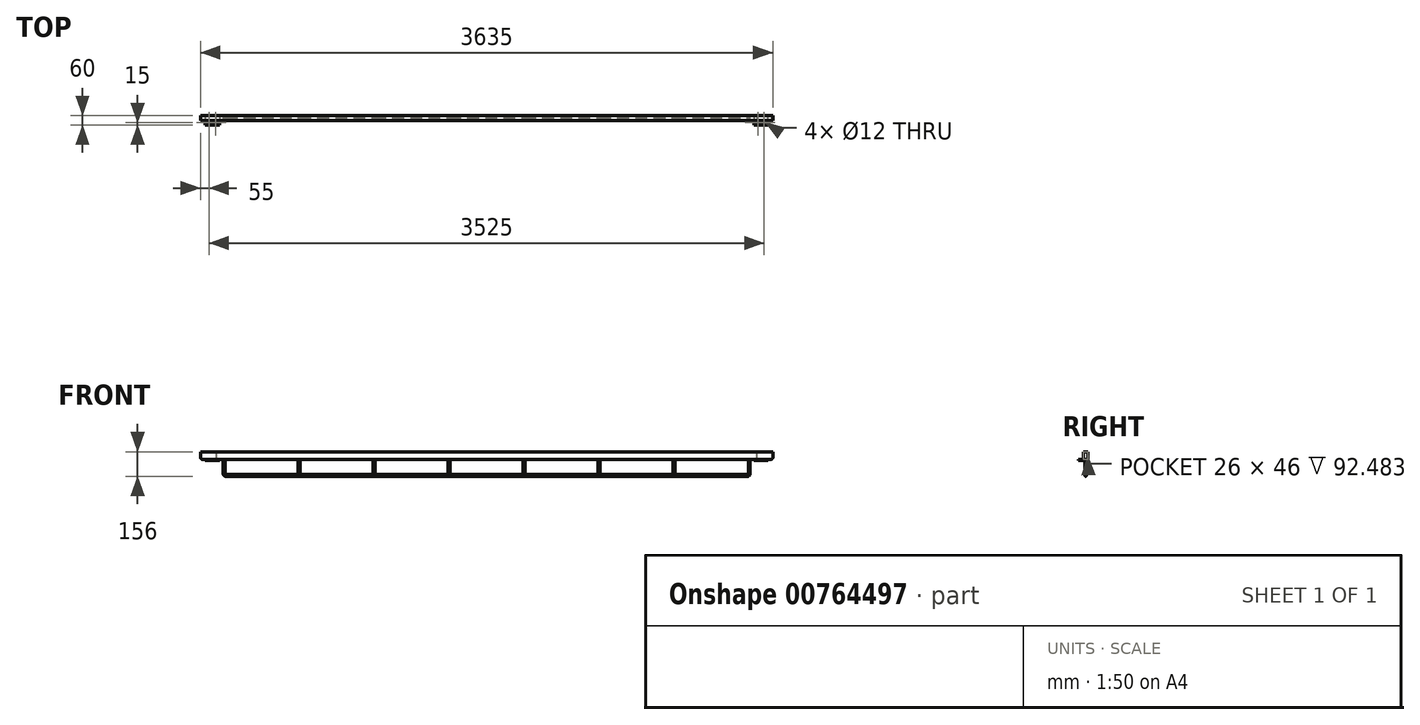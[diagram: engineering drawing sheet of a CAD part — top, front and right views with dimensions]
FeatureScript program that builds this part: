
annotation { "Feature Type Name" : "Feature", "Feature Type Description" : "" }
export const myFeature = defineFeature(function(context is Context, id is Id, definition is map)
    precondition{}
    {
        {
            var Q0;
            Q0=qCreatedBy(makeId("Front.planeOp"),FACE);
            var sketch = newSketch(context, id + "F0", { "sketchPlane" : qUnion([Q0])});
            skLineSegment(sketch, "E0.bottom", {"start": v(1787.5, -25) * mm, "end": v(-1787.5, -25) * mm});
            skLineSegment(sketch, "E0.top", {"start": v(1787.5, 25) * mm, "end": v(-1787.5, 25) * mm});
            skLineSegment(sketch, "E0.left", {"start": v(1787.5, -25) * mm, "end": v(1787.5, 25) * mm});
            skLineSegment(sketch, "E0.right", {"start": v(-1787.5, -25) * mm, "end": v(-1787.5, 25) * mm});
            skPoint(sketch, "E0.middle", {"position": v(0, 0) * mm});
            skSolve(sketch);
        }
        {
            var Q0;
            Q0 = qSketchRegion(id + "F0", true);
            extrude(context, id + "F1", {"entities" : qUnion([Q0]), "depth" : 15 * mm, "offsetDistance" : 25 * mm, "hasSecondDirection" : true, "secondDirectionOppositeDirection" : true, "secondDirectionDepth" : 15 * mm});
        }
        {
            var Q0;
            Q0=makeQuery(id+"F1.opExtrude","SWEPT_FACE",FACE,{"disambiguationData":[OSD([sQuery(id+"F0.wireOp",EDGE,"E0.bottom")])]});
            var sketch = newSketch(context, id + "F2", { "sketchPlane" : qUnion([Q0])});
            skLineSegment(sketch, "E1.0", {"start": v(-1787.5, 15) * mm, "end": v(-1787.5, -15) * mm});
            skLineSegment(sketch, "E2.bottom", {"start": v(-1787.5, -15) * mm, "end": v(-1697.5, -15) * mm});
            skLineSegment(sketch, "E2.top", {"start": v(-1787.5, 45) * mm, "end": v(-1697.5, 45) * mm});
            skLineSegment(sketch, "E2.left", {"start": v(-1787.5, -15) * mm, "end": v(-1787.5, 45) * mm});
            skLineSegment(sketch, "E2.right", {"start": v(-1697.5, -15) * mm, "end": v(-1697.5, 45) * mm});
            skSolve(sketch);
        }
        {
            var Q0;
            Q0 = qSketchRegion(id + "F2", true);
            extrude(context, id + "F3", {"entities" : qUnion([Q0]), "operationType" : NewBodyOperationType.ADD, "depth" : 5 * mm, "offsetDistance" : 25 * mm});
        }
        {
            var Q0;
            Q0=makeQuery(id+"F1.opExtrude","SWEPT_FACE",FACE,{"disambiguationData":[OSD([sQuery(id+"F0.wireOp",EDGE,"E0.bottom")])]});
            var sketch = newSketch(context, id + "F4", { "sketchPlane" : qUnion([Q0])});
            skLineSegment(sketch, "E3.0", {"start": v(1787.5, 15) * mm, "end": v(1787.5, -15) * mm});
            skLineSegment(sketch, "E4.bottom", {"start": v(1787.5, -15) * mm, "end": v(1697.5, -15) * mm});
            skLineSegment(sketch, "E4.top", {"start": v(1787.5, 45) * mm, "end": v(1697.5, 45) * mm});
            skLineSegment(sketch, "E4.left", {"start": v(1787.5, -15) * mm, "end": v(1787.5, 45) * mm});
            skLineSegment(sketch, "E4.right", {"start": v(1697.5, -15) * mm, "end": v(1697.5, 45) * mm});
            skSolve(sketch);
        }
        {
            var Q0;
            Q0 = qSketchRegion(id + "F4", true);
            extrude(context, id + "F5", {"entities" : qUnion([Q0]), "operationType" : NewBodyOperationType.ADD, "depth" : 5 * mm, "offsetDistance" : 25 * mm});
        }
        {
            var Q0;
            Q0=makeQuery(id+"F3.opExtrude","CAP_FACE",FACE,{"disambiguationData":[OSD([sQuery(id+"F2.wireOp",EDGE,"E2.bottom"),sQuery(id+"F2.wireOp",EDGE,"E2.top"),sQuery(id+"F2.wireOp",EDGE,"E2.left"),sQuery(id+"F2.wireOp",EDGE,"E2.right")])],"isStart":false});
            var sketch = newSketch(context, id + "F6", { "sketchPlane" : qUnion([Q0])});
            skCircle(sketch, "E5.0", {"center": v(-935, 30) * mm, "radius": 6 * mm});
            skCircle(sketch, "E6.0", {"center": v(-975, 30) * mm, "radius": 6 * mm});
            skSolve(sketch);
        }
        {
            var Q0;
            Q0 = qSketchRegion(id + "F6", true);
            var Q1;
            Q1=makeQuery(id+"F3.opExtrude","CAP_FACE",FACE,{"disambiguationData":[OSD([sQuery(id+"F2.wireOp",EDGE,"E2.bottom"),sQuery(id+"F2.wireOp",EDGE,"E2.top"),sQuery(id+"F2.wireOp",EDGE,"E2.left"),sQuery(id+"F2.wireOp",EDGE,"E2.right")])],"isStart":true});
            extrude(context, id + "F7", {"entities" : qUnion([Q0]), "operationType" : NewBodyOperationType.REMOVE, "endBound" : BoundingType.UP_TO_SURFACE, "oppositeDirection" : true, "depth" : 25 * mm, "endBoundEntityFace" : qUnion([Q1]), "offsetDistance" : 25 * mm});
        }
        {
            var Q0;
            Q0=makeQuery(id+"F5.opExtrude","CAP_FACE",FACE,{"disambiguationData":[OSD([sQuery(id+"F4.wireOp",EDGE,"E4.bottom"),sQuery(id+"F4.wireOp",EDGE,"E4.top"),sQuery(id+"F4.wireOp",EDGE,"E4.left"),sQuery(id+"F4.wireOp",EDGE,"E4.right")])],"isStart":false});
            var sketch = newSketch(context, id + "F8", { "sketchPlane" : qUnion([Q0])});
            skCircle(sketch, "E7.0", {"center": v(1762.5, 30) * mm, "radius": 6 * mm});
            skCircle(sketch, "E8.0", {"center": v(1722.5, 30) * mm, "radius": 6 * mm});
            skSolve(sketch);
        }
        {
            var Q0;
            Q0 = qSketchRegion(id + "F8", true);
            var Q1;
            Q1=makeQuery(id+"F5.opExtrude","CAP_FACE",FACE,{"disambiguationData":[OSD([sQuery(id+"F4.wireOp",EDGE,"E4.bottom"),sQuery(id+"F4.wireOp",EDGE,"E4.top"),sQuery(id+"F4.wireOp",EDGE,"E4.left"),sQuery(id+"F4.wireOp",EDGE,"E4.right")])],"isStart":true});
            extrude(context, id + "F9", {"entities" : qUnion([Q0]), "operationType" : NewBodyOperationType.REMOVE, "endBound" : BoundingType.UP_TO_SURFACE, "oppositeDirection" : true, "depth" : 25 * mm, "endBoundEntityFace" : qUnion([Q1]), "offsetDistance" : 25 * mm});
        }
        {
            var Q0;
            Q0=makeQuery(id+"F1.opExtrude","SWEPT_FACE",FACE,{"disambiguationData":[OSD([sQuery(id+"F0.wireOp",EDGE,"E0.bottom")])]});
            var sketch = newSketch(context, id + "F10", { "sketchPlane" : qUnion([Q0])});
            skLineSegment(sketch, "E9", {"start": v(-1697.5, -15) * mm, "end": v(-1667.5, -15) * mm, "construction": true});
            skLineSegment(sketch, "E10", {"start": v(-1667.5, -15) * mm, "end": v(-1667.5, 15) * mm, "construction": true});
            skCircle(sketch, "E11", {"center": v(-1667.5, 0) * mm, "radius": 6 * mm});
            skLineSegment(sketch, "E12", {"start": v(1697.5, -15) * mm, "end": v(1667.5, -15) * mm, "construction": true});
            skLineSegment(sketch, "E13", {"start": v(1667.5, -15) * mm, "end": v(1667.5, 15) * mm, "construction": true});
            skCircle(sketch, "E14", {"center": v(1667.5, 0) * mm, "radius": 6 * mm});
            skLineSegment(sketch, "E15", {"start": v(1667.5, 0) * mm, "end": v(1191.07, 0) * mm});
            skLineSegment(sketch, "E16", {"start": v(1191.07, 0) * mm, "end": v(714.64, 0) * mm});
            skLineSegment(sketch, "E17", {"start": v(714.64, 0) * mm, "end": v(238.21, 0) * mm});
            skLineSegment(sketch, "E18", {"start": v(238.21, 0) * mm, "end": v(-238.21, 0) * mm});
            skLineSegment(sketch, "E19", {"start": v(-238.21, 0) * mm, "end": v(-714.64, 0) * mm});
            skLineSegment(sketch, "E20", {"start": v(-714.64, 0) * mm, "end": v(-1191.07, 0) * mm});
            skLineSegment(sketch, "E21", {"start": v(-1667.5, 0) * mm, "end": v(-1191.07, 0) * mm});
            skCircle(sketch, "E22", {"center": v(-1191.07, 0) * mm, "radius": 6 * mm});
            skCircle(sketch, "E23", {"center": v(-714.64, 0) * mm, "radius": 6 * mm});
            skCircle(sketch, "E24", {"center": v(-238.21, 0) * mm, "radius": 6 * mm});
            skCircle(sketch, "E25", {"center": v(238.21, 0) * mm, "radius": 6 * mm});
            skCircle(sketch, "E26", {"center": v(714.64, 0) * mm, "radius": 6 * mm});
            skCircle(sketch, "E27", {"center": v(1191.07, 0) * mm, "radius": 6 * mm});
            skSolve(sketch);
        }
        {
            var Q0;
            Q0=qCreatedBy(makeId("Front.planeOp"),FACE);
            var sketch = newSketch(context, id + "F11", { "sketchPlane" : qUnion([Q0])});
            skLineSegment(sketch, "E28.0", {"start": v(-1667.5, -25) * mm, "end": v(-1191.07, -25) * mm});
            skLineSegment(sketch, "E29.0", {"start": v(-714.64, -25) * mm, "end": v(-1191.07, -25) * mm});
            skLineSegment(sketch, "E30.0", {"start": v(-238.21, -25) * mm, "end": v(-714.64, -25) * mm});
            skLineSegment(sketch, "E31.0", {"start": v(238.21, -25) * mm, "end": v(-238.21, -25) * mm});
            skLineSegment(sketch, "E32.0", {"start": v(714.64, -25) * mm, "end": v(238.21, -25) * mm});
            skLineSegment(sketch, "E33.0", {"start": v(1191.07, -25) * mm, "end": v(714.64, -25) * mm});
            skLineSegment(sketch, "E34.0", {"start": v(1667.5, -25) * mm, "end": v(1191.07, -25) * mm});
            skLineSegment(sketch, "E35", {"start": v(1667.5, -25) * mm, "end": v(1667.5, -115) * mm});
            skLineSegment(sketch, "E36", {"start": v(1667.5, -115) * mm, "end": v(1657.5, -115) * mm});
            skArc(sketch, "E37", {"start": v(1657.5, -125) * mm, "mid": v(1664.57, -122.07) * mm, "end": v(1667.5, -115) * mm});
            skLineSegment(sketch, "E38", {"start": v(1657.5, -115) * mm, "end": v(1657.5, -125) * mm, "construction": true});
            skLineSegment(sketch, "E39", {"start": v(-1667.5, -25) * mm, "end": v(-1667.5, -115) * mm});
            skLineSegment(sketch, "E40", {"start": v(-1667.5, -115) * mm, "end": v(-1657.5, -115) * mm});
            skArc(sketch, "E41", {"start": v(-1667.5, -115) * mm, "mid": v(-1664.57, -122.07) * mm, "end": v(-1657.5, -125) * mm});
            skLineSegment(sketch, "E42", {"start": v(-1657.5, -115) * mm, "end": v(-1657.5, -125) * mm, "construction": true});
            skLineSegment(sketch, "E43", {"start": v(-1657.5, -125) * mm, "end": v(1657.5, -125) * mm});
            skLineSegment(sketch, "E44", {"start": v(1191.07, -25) * mm, "end": v(1191.07, -125) * mm});
            skLineSegment(sketch, "E45", {"start": v(714.64, -25) * mm, "end": v(714.64, -125) * mm});
            skLineSegment(sketch, "E46", {"start": v(238.21, -25) * mm, "end": v(238.21, -125) * mm});
            skLineSegment(sketch, "E47", {"start": v(-238.21, -25) * mm, "end": v(-238.21, -125) * mm});
            skLineSegment(sketch, "E48", {"start": v(-714.64, -25) * mm, "end": v(-714.64, -125) * mm});
            skLineSegment(sketch, "E49", {"start": v(-1191.07, -25) * mm, "end": v(-1191.07, -125) * mm});
            skSolve(sketch);
        }
        {
            var Q0;
            Q0=makeQuery(id+"F10.imprint","IMPRINT",FACE,{"disambiguationData":[TD([[makeQuery(id+"F10.imprint","IMPRINT",EDGE,{"derivedFrom":sQuery(id+"F10.wireOp",EDGE,"E11")}),1.0]])]});
            var Q1;
            Q1=sQuery(id+"F11.wireOp",EDGE,"E39");
            var Q2;
            Q2=sQuery(id+"F11.wireOp",EDGE,"E41");
            var Q3;
            Q3=sQuery(id+"F11.wireOp",EDGE,"E43");
            var Q4;
            Q4=sQuery(id+"F11.wireOp",EDGE,"E37");
            var Q5;
            Q5=sQuery(id+"F11.wireOp",EDGE,"E35");
            sweep(context, id + "F12", {"operationType" : NewBodyOperationType.ADD, "profiles" : qUnion([Q0]), "path" : qUnion([Q1, Q2, Q3, Q4, Q5])});
        }
        {
            var Q0;
            {var subQ0=sQuery(id+"F10.wireOp",EDGE,"E21");var subQ1=sQuery(id+"F10.wireOp",EDGE,"E20");var subQ2=makeQuery(id+"F10.imprint","INTERSECT",VERTEX,{"derivedFrom":[subQ1,subQ0]});Q0=makeQuery(id+"F10.imprint","IMPRINT",FACE,{"disambiguationData":[TD([[makeQuery(id+"F10.imprint","IMPRINT",EDGE,{"disambiguationData":[TD([[subQ2,1.0]])],"derivedFrom":subQ1}),1.0]])]});}
            var Q1;
            {var subQ0=sQuery(id+"F10.wireOp",EDGE,"E21");var subQ1=sQuery(id+"F10.wireOp",EDGE,"E20");var subQ2=makeQuery(id+"F10.imprint","INTERSECT",VERTEX,{"derivedFrom":[subQ1,subQ0]});Q1=makeQuery(id+"F10.imprint","IMPRINT",FACE,{"disambiguationData":[TD([[makeQuery(id+"F10.imprint","IMPRINT",EDGE,{"disambiguationData":[TD([[subQ2,1.0]])],"derivedFrom":subQ1}),-1.0]])]});}
            var Q2;
            Q2=sQuery(id+"F11.wireOp",EDGE,"E49");
            sweep(context, id + "F13", {"operationType" : NewBodyOperationType.ADD, "profiles" : qUnion([Q0, Q1]), "path" : qUnion([Q2])});
        }
        {
            var Q0;
            {var subQ0=sQuery(id+"F10.wireOp",EDGE,"E20");var subQ1=sQuery(id+"F10.wireOp",EDGE,"E19");var subQ2=makeQuery(id+"F10.imprint","INTERSECT",VERTEX,{"derivedFrom":[subQ1,subQ0]});Q0=makeQuery(id+"F10.imprint","IMPRINT",FACE,{"disambiguationData":[TD([[makeQuery(id+"F10.imprint","IMPRINT",EDGE,{"disambiguationData":[TD([[subQ2,1.0]])],"derivedFrom":subQ1}),-1.0]])]});}
            var Q1;
            {var subQ0=sQuery(id+"F10.wireOp",EDGE,"E20");var subQ1=sQuery(id+"F10.wireOp",EDGE,"E19");var subQ2=makeQuery(id+"F10.imprint","INTERSECT",VERTEX,{"derivedFrom":[subQ1,subQ0]});Q1=makeQuery(id+"F10.imprint","IMPRINT",FACE,{"disambiguationData":[TD([[makeQuery(id+"F10.imprint","IMPRINT",EDGE,{"disambiguationData":[TD([[subQ2,1.0]])],"derivedFrom":subQ1}),1.0]])]});}
            var Q2;
            Q2=sQuery(id+"F11.wireOp",EDGE,"E48");
            sweep(context, id + "F14", {"operationType" : NewBodyOperationType.ADD, "profiles" : qUnion([Q0, Q1]), "path" : qUnion([Q2])});
        }
        {
            var Q0;
            {var subQ0=sQuery(id+"F10.wireOp",EDGE,"E19");var subQ1=sQuery(id+"F10.wireOp",EDGE,"E18");var subQ2=makeQuery(id+"F10.imprint","INTERSECT",VERTEX,{"derivedFrom":[subQ1,subQ0]});Q0=makeQuery(id+"F10.imprint","IMPRINT",FACE,{"disambiguationData":[TD([[makeQuery(id+"F10.imprint","IMPRINT",EDGE,{"disambiguationData":[TD([[subQ2,1.0]])],"derivedFrom":subQ1}),-1.0]])]});}
            var Q1;
            {var subQ0=sQuery(id+"F10.wireOp",EDGE,"E19");var subQ1=sQuery(id+"F10.wireOp",EDGE,"E18");var subQ2=makeQuery(id+"F10.imprint","INTERSECT",VERTEX,{"derivedFrom":[subQ1,subQ0]});Q1=makeQuery(id+"F10.imprint","IMPRINT",FACE,{"disambiguationData":[TD([[makeQuery(id+"F10.imprint","IMPRINT",EDGE,{"disambiguationData":[TD([[subQ2,1.0]])],"derivedFrom":subQ1}),1.0]])]});}
            var Q2;
            Q2=sQuery(id+"F11.wireOp",EDGE,"E47");
            sweep(context, id + "F15", {"operationType" : NewBodyOperationType.ADD, "profiles" : qUnion([Q0, Q1]), "path" : qUnion([Q2])});
        }
        {
            var Q0;
            Q0=makeQuery(id+"F10.imprint","IMPRINT",FACE,{"disambiguationData":[TD([[makeQuery(id+"F10.imprint","IMPRINT",EDGE,{"derivedFrom":sQuery(id+"F10.wireOp",EDGE,"E11")}),1.0]])]});
            var Q1;
            Q1=sQuery(id+"F11.wireOp",EDGE,"E39");
            var Q2;
            Q2=sQuery(id+"F11.wireOp",EDGE,"E41");
            var Q3;
            Q3=sQuery(id+"F11.wireOp",EDGE,"E43");
            var Q4;
            Q4=sQuery(id+"F11.wireOp",EDGE,"E37");
            sweep(context, id + "F16", {"operationType" : NewBodyOperationType.ADD, "profiles" : qUnion([Q0]), "path" : qUnion([Q1, Q2, Q3, Q4])});
        }
        {
            var Q0;
            {var subQ0=sQuery(id+"F10.wireOp",EDGE,"E18");var subQ1=sQuery(id+"F10.wireOp",EDGE,"E17");var subQ2=makeQuery(id+"F10.imprint","INTERSECT",VERTEX,{"derivedFrom":[subQ1,subQ0]});Q0=makeQuery(id+"F10.imprint","IMPRINT",FACE,{"disambiguationData":[TD([[makeQuery(id+"F10.imprint","IMPRINT",EDGE,{"disambiguationData":[TD([[subQ2,1.0]])],"derivedFrom":subQ1}),-1.0]])]});}
            var Q1;
            {var subQ0=sQuery(id+"F10.wireOp",EDGE,"E18");var subQ1=sQuery(id+"F10.wireOp",EDGE,"E17");var subQ2=makeQuery(id+"F10.imprint","INTERSECT",VERTEX,{"derivedFrom":[subQ1,subQ0]});Q1=makeQuery(id+"F10.imprint","IMPRINT",FACE,{"disambiguationData":[TD([[makeQuery(id+"F10.imprint","IMPRINT",EDGE,{"disambiguationData":[TD([[subQ2,1.0]])],"derivedFrom":subQ1}),1.0]])]});}
            var Q2;
            Q2=sQuery(id+"F11.wireOp",EDGE,"E46");
            sweep(context, id + "F17", {"operationType" : NewBodyOperationType.ADD, "profiles" : qUnion([Q0, Q1]), "path" : qUnion([Q2])});
        }
        {
            var Q0;
            {var subQ0=sQuery(id+"F10.wireOp",EDGE,"E17");var subQ1=sQuery(id+"F10.wireOp",EDGE,"E16");var subQ2=makeQuery(id+"F10.imprint","INTERSECT",VERTEX,{"derivedFrom":[subQ1,subQ0]});Q0=makeQuery(id+"F10.imprint","IMPRINT",FACE,{"disambiguationData":[TD([[makeQuery(id+"F10.imprint","IMPRINT",EDGE,{"disambiguationData":[TD([[subQ2,1.0]])],"derivedFrom":subQ1}),-1.0]])]});}
            var Q1;
            {var subQ0=sQuery(id+"F10.wireOp",EDGE,"E17");var subQ1=sQuery(id+"F10.wireOp",EDGE,"E16");var subQ2=makeQuery(id+"F10.imprint","INTERSECT",VERTEX,{"derivedFrom":[subQ1,subQ0]});Q1=makeQuery(id+"F10.imprint","IMPRINT",FACE,{"disambiguationData":[TD([[makeQuery(id+"F10.imprint","IMPRINT",EDGE,{"disambiguationData":[TD([[subQ2,1.0]])],"derivedFrom":subQ1}),1.0]])]});}
            var Q2;
            Q2=sQuery(id+"F11.wireOp",EDGE,"E45");
            sweep(context, id + "F18", {"operationType" : NewBodyOperationType.ADD, "profiles" : qUnion([Q0, Q1]), "path" : qUnion([Q2])});
        }
        {
            var Q0;
            {var subQ0=sQuery(id+"F10.wireOp",EDGE,"E16");var subQ1=sQuery(id+"F10.wireOp",EDGE,"E15");var subQ2=makeQuery(id+"F10.imprint","INTERSECT",VERTEX,{"derivedFrom":[subQ1,subQ0]});Q0=makeQuery(id+"F10.imprint","IMPRINT",FACE,{"disambiguationData":[TD([[makeQuery(id+"F10.imprint","IMPRINT",EDGE,{"disambiguationData":[TD([[subQ2,1.0]])],"derivedFrom":subQ1}),1.0]])]});}
            var Q1;
            {var subQ0=sQuery(id+"F10.wireOp",EDGE,"E16");var subQ1=sQuery(id+"F10.wireOp",EDGE,"E15");var subQ2=makeQuery(id+"F10.imprint","INTERSECT",VERTEX,{"derivedFrom":[subQ1,subQ0]});Q1=makeQuery(id+"F10.imprint","IMPRINT",FACE,{"disambiguationData":[TD([[makeQuery(id+"F10.imprint","IMPRINT",EDGE,{"disambiguationData":[TD([[subQ2,1.0]])],"derivedFrom":subQ1}),-1.0]])]});}
            var Q2;
            Q2=sQuery(id+"F11.wireOp",EDGE,"E44");
            sweep(context, id + "F19", {"operationType" : NewBodyOperationType.ADD, "profiles" : qUnion([Q0, Q1]), "path" : qUnion([Q2])});
        }
        {
            var Q0;
            Q0=makeQuery(id+"F3.opExtrude","CAP_FACE",FACE,{"disambiguationData":[OSD([sQuery(id+"F2.wireOp",EDGE,"E2.bottom"),sQuery(id+"F2.wireOp",EDGE,"E2.top"),sQuery(id+"F2.wireOp",EDGE,"E2.left"),sQuery(id+"F2.wireOp",EDGE,"E2.right")])],"isStart":false});
            var sketch = newSketch(context, id + "F20", { "sketchPlane" : qUnion([Q0])});
            skLineSegment(sketch, "E50.bottom", {"start": v(-1787.5, 45) * mm, "end": v(-1762.5, 45) * mm, "construction": true});
            skLineSegment(sketch, "E50.top", {"start": v(-1787.5, 30) * mm, "end": v(-1762.5, 30) * mm});
            skLineSegment(sketch, "E50.left", {"start": v(-1787.5, 45) * mm, "end": v(-1787.5, 30) * mm});
            skLineSegment(sketch, "E50.right", {"start": v(-1762.5, 45) * mm, "end": v(-1762.5, 30) * mm});
            skLineSegment(sketch, "E51", {"start": v(-1762.5, 30) * mm, "end": v(-1722.5, 30) * mm});
            skCircle(sketch, "E52", {"center": v(-1762.5, 30) * mm, "radius": 6 * mm});
            skCircle(sketch, "E53", {"center": v(-1722.5, 30) * mm, "radius": 6 * mm});
            skSolve(sketch);
        }
        {
            var Q0;
            Q0 = qSketchRegion(id + "F20", true);
            extrude(context, id + "F21", {"entities" : qUnion([Q0]), "operationType" : NewBodyOperationType.REMOVE, "endBound" : BoundingType.UP_TO_NEXT, "oppositeDirection" : true, "depth" : 25 * mm, "offsetDistance" : 25 * mm});
        }
        {
            var Q0;
            Q0=makeQuery(id+"F5.boolean.opBoolean","MERGE",FACE,{"derivedFrom":[makeQuery(id+"F1.opExtrude","SWEPT_FACE",FACE,{"disambiguationData":[OSD([sQuery(id+"F0.wireOp",EDGE,"E0.left")])]}),makeQuery(id+"F5.opExtrude","SWEPT_FACE",FACE,{"disambiguationData":[OSD([sQuery(id+"F4.wireOp",EDGE,"E4.left")])]})]});
            var sketch = newSketch(context, id + "F22", { "sketchPlane" : qUnion([Q0])});
            skLineSegment(sketch, "E54.bottom", {"start": v(-15, 25) * mm, "end": v(15, 25) * mm});
            skLineSegment(sketch, "E54.top", {"start": v(-15, -25) * mm, "end": v(15, -25) * mm});
            skLineSegment(sketch, "E54.left", {"start": v(-15, 25) * mm, "end": v(-15, -25) * mm});
            skLineSegment(sketch, "E54.right", {"start": v(15, 25) * mm, "end": v(15, -25) * mm});
            skSolve(sketch);
        }
        {
            var Q0;
            Q0 = qSketchRegion(id + "F22", true);
            extrude(context, id + "F23", {"entities" : qUnion([Q0]), "operationType" : NewBodyOperationType.ADD, "depth" : 30 * mm, "offsetDistance" : 25 * mm});
        }
        {
            var Q0;
            Q0=makeQuery(id+"F23.opExtrude","CAP_EDGE",EDGE,{"disambiguationData":[OSD([sQuery(id+"F22.wireOp",EDGE,"E54.top")])],"isStart":false});
            fillet(context, id + "F24", {"entities" : qUnion([Q0]), "radius" : 15 * mm, "tangentPropagation" : true, "allowEdgeOverflow" : false});
        }
        {
            var Q0;
            Q0=makeQuery(id+"F23.opExtrude","CAP_FACE",FACE,{"disambiguationData":[OSD([sQuery(id+"F22.wireOp",EDGE,"E54.bottom"),sQuery(id+"F22.wireOp",EDGE,"E54.top"),sQuery(id+"F22.wireOp",EDGE,"E54.left"),sQuery(id+"F22.wireOp",EDGE,"E54.right")])],"isStart":false});
            var sketch = newSketch(context, id + "F25", { "sketchPlane" : qUnion([Q0])});
            skLineSegment(sketch, "E55.bottom", {"start": v(-15, 25) * mm, "end": v(15, 25) * mm});
            skLineSegment(sketch, "E55.top", {"start": v(-15, -25) * mm, "end": v(15, -25) * mm});
            skLineSegment(sketch, "E55.left", {"start": v(-15, 25) * mm, "end": v(-15, -25) * mm});
            skLineSegment(sketch, "E55.right", {"start": v(15, 25) * mm, "end": v(15, -25) * mm});
            skLineSegment(sketch, "E56", {"start": v(-15, -25) * mm, "end": v(15, 25) * mm, "construction": true});
            skLineSegment(sketch, "E57.bottom", {"start": v(13, -23) * mm, "end": v(-13, -23) * mm});
            skLineSegment(sketch, "E57.top", {"start": v(13, 23) * mm, "end": v(-13, 23) * mm});
            skLineSegment(sketch, "E57.left", {"start": v(13, -23) * mm, "end": v(13, 23) * mm});
            skLineSegment(sketch, "E57.right", {"start": v(-13, -23) * mm, "end": v(-13, 23) * mm});
            skPoint(sketch, "E57.middle", {"position": v(0, 0) * mm});
            skSolve(sketch);
        }
        {
            var Q0;
            {var subQ0=sQuery(id+"F25.wireOp",EDGE,"E57.bottom");Q0=makeQuery(id+"F25.imprint","IMPRINT",FACE,{"disambiguationData":[TD([[makeQuery(id+"F25.imprint","IMPRINT",EDGE,{"derivedFrom":subQ0}),-1.0]])]});}
            var Q1;
            {var subQ0=sQuery(id+"F25.wireOp",EDGE,"E57.top");Q1=makeQuery(id+"F25.imprint","IMPRINT",FACE,{"disambiguationData":[TD([[makeQuery(id+"F25.imprint","IMPRINT",EDGE,{"derivedFrom":subQ0}),1.0]])]});}
            extrude(context, id + "F26", {"entities" : qUnion([Q0, Q1]), "operationType" : NewBodyOperationType.REMOVE, "oppositeDirection" : true, "depth" : 100 * mm, "offsetDistance" : 25 * mm});
        }
        {
            var Q0;
            Q0=makeQuery(id+"F3.boolean.opBoolean","MERGE",FACE,{"derivedFrom":[makeQuery(id+"F1.opExtrude","SWEPT_FACE",FACE,{"disambiguationData":[OSD([sQuery(id+"F0.wireOp",EDGE,"E0.right")])]}),makeQuery(id+"F3.opExtrude","SWEPT_FACE",FACE,{"disambiguationData":[OSD([sQuery(id+"F2.wireOp",EDGE,"E2.left")])]})]});
            var sketch = newSketch(context, id + "F27", { "sketchPlane" : qUnion([Q0])});
            skLineSegment(sketch, "E58.bottom", {"start": v(-15, 25) * mm, "end": v(15, 25) * mm});
            skLineSegment(sketch, "E58.top", {"start": v(-15, -25) * mm, "end": v(15, -25) * mm});
            skLineSegment(sketch, "E58.left", {"start": v(-15, 25) * mm, "end": v(-15, -25) * mm});
            skLineSegment(sketch, "E58.right", {"start": v(15, 25) * mm, "end": v(15, -25) * mm});
            skSolve(sketch);
        }
        {
            var Q0;
            Q0 = qSketchRegion(id + "F27", true);
            extrude(context, id + "F28", {"entities" : qUnion([Q0]), "operationType" : NewBodyOperationType.ADD, "depth" : 30 * mm, "offsetDistance" : 25 * mm});
        }
        {
            var Q0;
            Q0=makeQuery(id+"F28.opExtrude","CAP_FACE",FACE,{"disambiguationData":[OSD([sQuery(id+"F27.wireOp",EDGE,"E58.bottom"),sQuery(id+"F27.wireOp",EDGE,"E58.top"),sQuery(id+"F27.wireOp",EDGE,"E58.left"),sQuery(id+"F27.wireOp",EDGE,"E58.right")])],"isStart":false});
            var sketch = newSketch(context, id + "F29", { "sketchPlane" : qUnion([Q0])});
            skLineSegment(sketch, "E59.bottom", {"start": v(-15, 25) * mm, "end": v(15, 25) * mm});
            skLineSegment(sketch, "E59.top", {"start": v(-15, -25) * mm, "end": v(15, -25) * mm});
            skLineSegment(sketch, "E59.left", {"start": v(-15, 25) * mm, "end": v(-15, -25) * mm});
            skLineSegment(sketch, "E59.right", {"start": v(15, 25) * mm, "end": v(15, -25) * mm});
            skLineSegment(sketch, "E60", {"start": v(15, -25) * mm, "end": v(-15, 25) * mm, "construction": true});
            skLineSegment(sketch, "E61.bottom", {"start": v(13, 23) * mm, "end": v(-13, 23) * mm});
            skLineSegment(sketch, "E61.top", {"start": v(13, -23) * mm, "end": v(-13, -23) * mm});
            skLineSegment(sketch, "E61.left", {"start": v(13, 23) * mm, "end": v(13, -23) * mm});
            skLineSegment(sketch, "E61.right", {"start": v(-13, 23) * mm, "end": v(-13, -23) * mm});
            skPoint(sketch, "E61.middle", {"position": v(0, 0) * mm});
            skSolve(sketch);
        }
        {
            var Q0;
            Q0=makeQuery(id+"F29.imprint","IMPRINT",FACE,{"disambiguationData":[TD([[makeQuery(id+"F29.imprint","IMPRINT",EDGE,{"derivedFrom":sQuery(id+"F29.wireOp",EDGE,"E61.bottom")}),1.0]])]});
            extrude(context, id + "F30", {"entities" : qUnion([Q0]), "operationType" : NewBodyOperationType.REMOVE, "oppositeDirection" : true, "depth" : 100 * mm, "offsetDistance" : 25 * mm});
        }
        {
            var Q0;
            Q0=makeQuery(id+"F28.opExtrude","CAP_EDGE",EDGE,{"disambiguationData":[OSD([sQuery(id+"F27.wireOp",EDGE,"E58.top")])],"isStart":false});
            fillet(context, id + "F31", {"entities" : qUnion([Q0]), "radius" : 15 * mm, "tangentPropagation" : true, "allowEdgeOverflow" : false});
        }
    });
